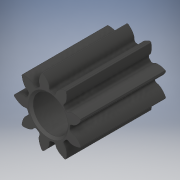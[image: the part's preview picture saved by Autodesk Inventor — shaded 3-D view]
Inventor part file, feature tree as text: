
AUTODESK INVENTOR PART (.ipt)
format: ipt  version: 2018 (Build 220112000, 112)  size: 216,576 bytes
history: native  units: in
note: dims shown in document units (in); Inventor stores cm internally (conversion verified against a paired STEP export)
features: chamfer x1
ambient origin geometry x8: Origin, YZ Plane, XZ Plane, XY Plane, X Axis, Y Axis, Z Axis, Center Point
bodies: Solid1 (feature_tree)
feature tree (1):
  chamfer  "Chamfer1"  [1 undecoded]
note: 1 required parameter value undecoded (feature->parameter linkage not recoverable at this tier; creation-order binding heuristic only, values carry confidence <= 0.55)
